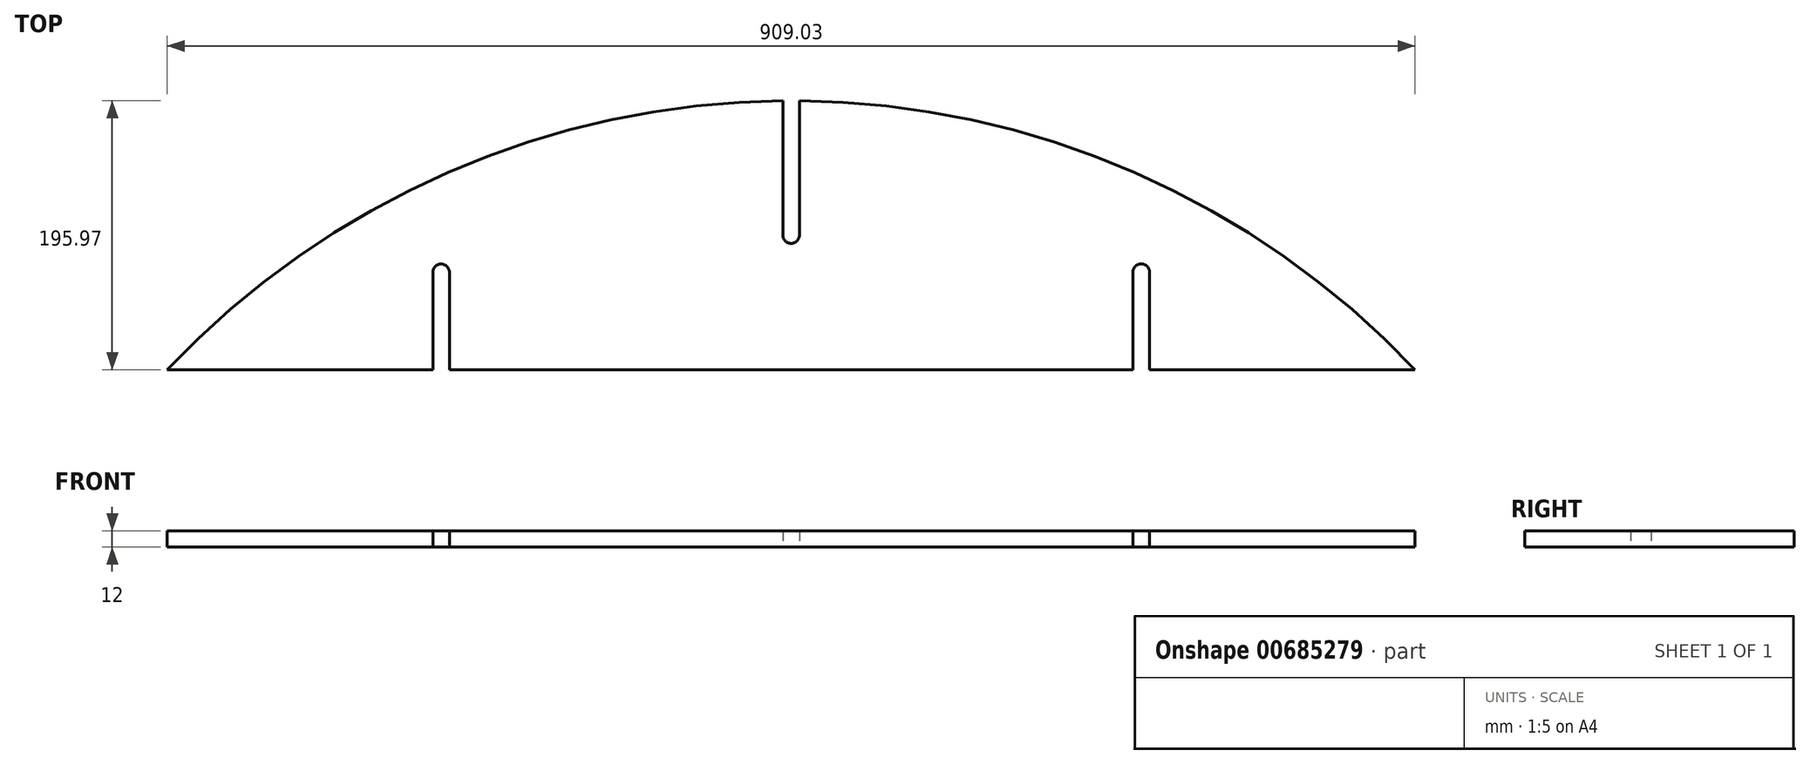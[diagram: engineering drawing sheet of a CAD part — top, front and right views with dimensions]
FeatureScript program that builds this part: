
annotation { "Feature Type Name" : "Feature", "Feature Type Description" : "" }
export const myFeature = defineFeature(function(context is Context, id is Id, definition is map)
    precondition{}
    {
        {
            var Q0;
            Q0=qCreatedBy(makeId("Top.planeOp"),FACE);
            var sketch = newSketch(context, id + "F0", { "sketchPlane" : qUnion([Q0])});
            skArc(sketch, "E0", {"start": v(909.03, 0) * mm, "mid": v(704.75, 143.72) * mm, "end": v(460.52, 195.97) * mm});
            skLineSegment(sketch, "E1", {"start": v(0, 0) * mm, "end": v(193.52, 0) * mm});
            skLineSegment(sketch, "E2", {"start": v(454.52, 252.18) * mm, "end": v(454.52, -138.83) * mm, "construction": true});
            skPoint(sketch, "E3", {"position": v(454.52, 0) * mm});
            skLineSegment(sketch, "E4", {"start": v(448.52, 195.97) * mm, "end": v(448.52, 98) * mm});
            skLineSegment(sketch, "E5", {"start": v(460.52, 98) * mm, "end": v(460.52, 195.97) * mm});
            skArc(sketch, "E6.trimOffspring", {"start": v(448.52, 195.97) * mm, "mid": v(204.28, 143.72) * mm, "end": v(0, 0) * mm});
            skLineSegment(sketch, "E7", {"start": v(199.52, -18.14) * mm, "end": v(199.52, 250.54) * mm, "construction": true});
            skLineSegment(sketch, "E8", {"start": v(193.52, 0) * mm, "end": v(193.52, 71) * mm});
            skLineSegment(sketch, "E9", {"start": v(205.52, 71) * mm, "end": v(205.52, 0) * mm});
            skLineSegment(sketch, "E10.MirrorCS", {"start": v(703.52, 71) * mm, "end": v(703.52, 0) * mm});
            skLineSegment(sketch, "E11.MirrorCS", {"start": v(715.52, 0) * mm, "end": v(715.52, 71) * mm});
            skLineSegment(sketch, "E12.trimOffspring", {"start": v(715.52, 0) * mm, "end": v(909.03, 0) * mm});
            skLineSegment(sketch, "E13.trimOffspring", {"start": v(205.52, 0) * mm, "end": v(703.52, 0) * mm});
            skArc(sketch, "E14", {"start": v(205.52, 71) * mm, "mid": v(199.52, 77) * mm, "end": v(193.52, 71) * mm});
            skArc(sketch, "E15", {"start": v(448.52, 98) * mm, "mid": v(454.52, 92) * mm, "end": v(460.52, 98) * mm});
            skArc(sketch, "E16", {"start": v(715.52, 71) * mm, "mid": v(709.52, 77) * mm, "end": v(703.52, 71) * mm});
            skSolve(sketch);
        }
        {
            var Q0;
            Q0=makeQuery(id+"F0.imprint","IMPRINT",FACE,{"disambiguationData":[TD([[makeQuery(id+"F0.imprint","IMPRINT",EDGE,{"derivedFrom":sQuery(id+"F0.wireOp",EDGE,"E0")}),1.0]])]});
            extrude(context, id + "F1", {"entities" : qUnion([Q0]), "depth" : 12 * mm, "offsetDistance" : 25 * mm});
        }
    });
